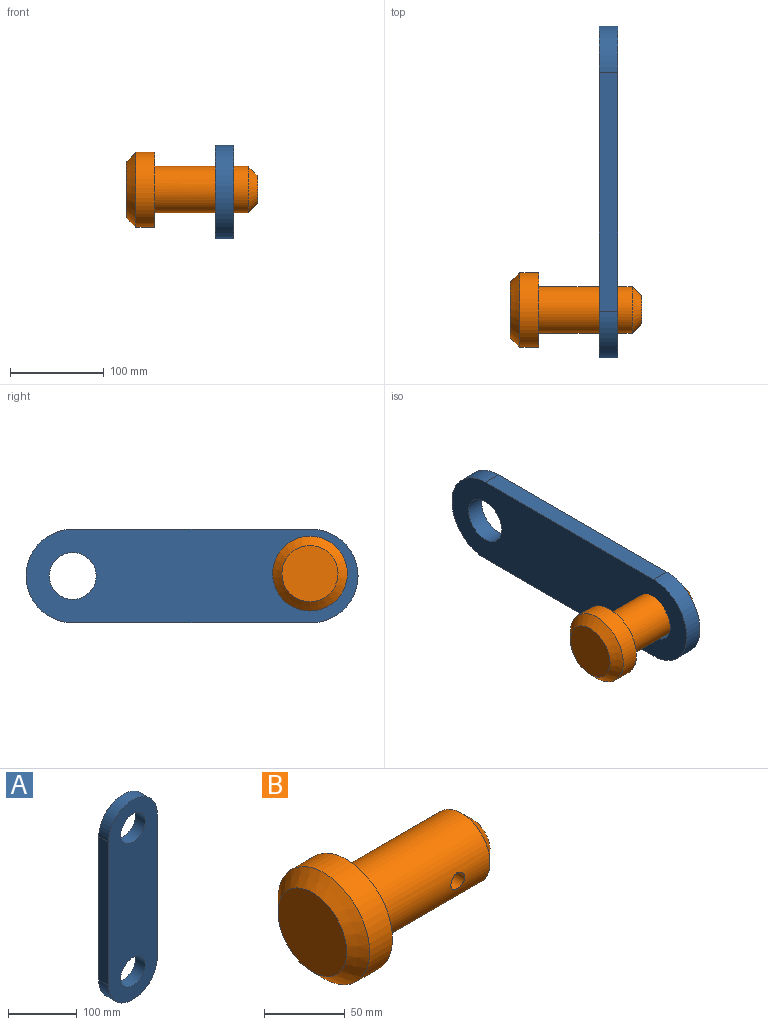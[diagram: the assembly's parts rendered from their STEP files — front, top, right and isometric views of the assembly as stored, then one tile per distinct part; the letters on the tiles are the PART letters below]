
ASSEMBLY  parts=2 mates=1
PART A: 8 faces, bbox 100x20x355 mm
  f0: plane 255x20mm, normal (1,0,0), area 5100mm2, adj f4,f5,f6,f7
  f1: cylinder r=25mm len=50mm, axis (0,1,0), area 3141.6mm2, adj f4,f5
  f2: cylinder r=25mm len=50mm, axis (0,1,0), area 3141.6mm2, adj f4,f5
  f3: plane 255x20mm, normal (-1,0,0), area 5100mm2, adj f4,f5,f6,f7
  f4: plane 355x100mm, normal (0,-1,0), area 29427mm2, adj f0,f1,f2,f3,f6,f7
  f5: plane 355x100mm, normal (0,1,0), area 29427mm2, adj f0,f1,f2,f3,f6,f7
  f6: cylinder r=50mm len=100mm, axis (0,1,0), area 3141.6mm2, adj f0,f3,f4,f5
  f7: cylinder r=50mm len=100mm, axis (0,-1,0), area 3141.6mm2, adj f0,f3,f4,f5
PART B: 8 faces, bbox 140.1x80x80 mm
  f0: cylinder r=25mm len=100.12mm, axis (1,0,0), area 15499.6mm2, adj f3,f4,f7
  f1: plane 60x60mm, normal (-1,0,0), area 2827.4mm2, adj f6
  f2: plane 30x30mm, normal (1,0,0), area 706.9mm2, adj f3
  f3: cone r=25mm half-angle=45deg, axis (-1,0,0), area 1777.2mm2, adj f0,f2
  f4: plane 80x80mm, normal (1,0,0), area 3063.1mm2, adj f0,f5
  f5: cylinder r=40mm len=80mm, axis (1,0,0), area 5026.5mm2, adj f4,f6
  f6: cone r=30mm half-angle=45deg, axis (1,0,0), area 3110mm2, adj f1,f5
  f7: cylinder r=6mm len=50mm, axis (0,-1,0), area 1857.5mm2, adj f0
PLACE A rot(axis=(0.58,0.58,-0.58),120deg) t=(-137.28,43.03,61.52)mm
PLACE B t=(154.42,-83.12,64.09)mm
MATE parallel A.f1 <-> B.f0  axis (1,0,0) through (-147.28,-84.47,61.52)mm
